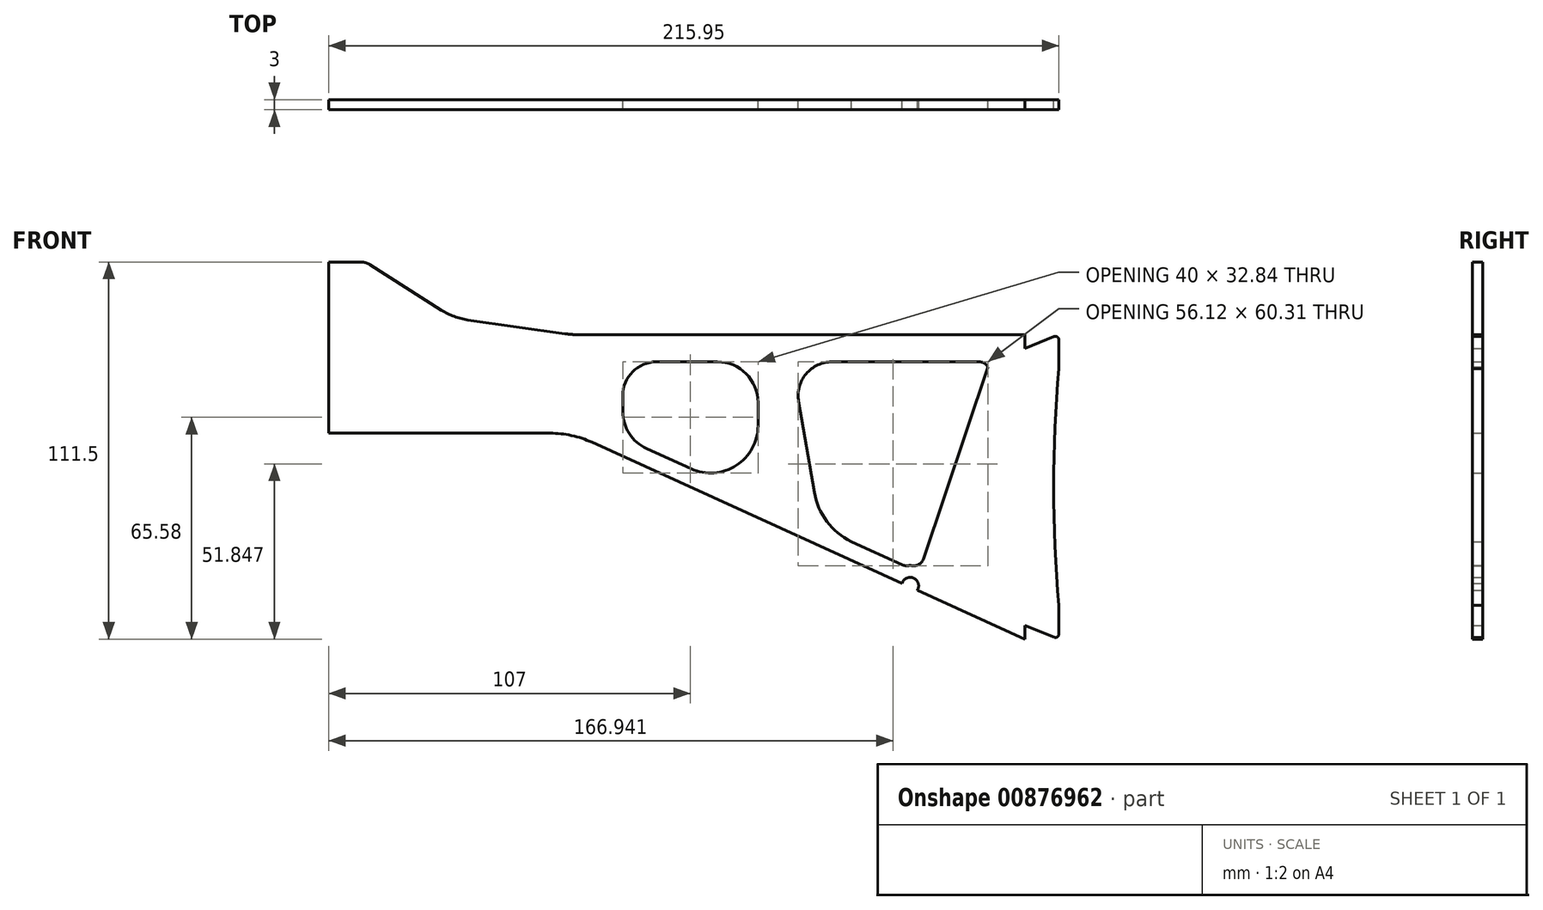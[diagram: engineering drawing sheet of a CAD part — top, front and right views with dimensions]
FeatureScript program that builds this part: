
annotation { "Feature Type Name" : "Feature", "Feature Type Description" : "" }
export const myFeature = defineFeature(function(context is Context, id is Id, definition is map)
    precondition{}
    {
        {
            var Q0;
            Q0=qCreatedBy(makeId("Front.planeOp"),FACE);
            var sketch = newSketch(context, id + "F0", { "sketchPlane" : qUnion([Q0])});
            skLineSegment(sketch, "E0", {"start": v(0, 0) * mm, "end": v(0, -50.6) * mm});
            skLineSegment(sketch, "E1", {"start": v(0, 0) * mm, "end": v(9.55, 0) * mm});
            skLineSegment(sketch, "E2", {"start": v(12.23, -0.78) * mm, "end": v(33.37, -14.2) * mm});
            skLineSegment(sketch, "E3", {"start": v(41.26, -17.1) * mm, "end": v(69.89, -21.2) * mm});
            skLineSegment(sketch, "E4", {"start": v(74.13, -21.5) * mm, "end": v(205.95, -21.5) * mm});
            skLineSegment(sketch, "E5", {"start": v(205.95, -21.5) * mm, "end": v(205.95, -25.5) * mm});
            skLineSegment(sketch, "E6", {"start": v(205.95, -25.5) * mm, "end": v(214.58, -22.05) * mm});
            skLineSegment(sketch, "E7", {"start": v(215.95, -22.98) * mm, "end": v(215.95, -31.5) * mm});
            skLineSegment(sketch, "E8", {"start": v(0, -50.6) * mm, "end": v(65.5, -50.6) * mm});
            skLineSegment(sketch, "E9", {"start": v(77.92, -53.3) * mm, "end": v(205.95, -111.5) * mm});
            skLineSegment(sketch, "E10", {"start": v(205.95, -111.5) * mm, "end": v(205.95, -107.5) * mm});
            skLineSegment(sketch, "E11", {"start": v(205.95, -107.5) * mm, "end": v(214.58, -110.95) * mm});
            skLineSegment(sketch, "E12", {"start": v(215.95, -110.02) * mm, "end": v(215.95, -101.5) * mm});
            skArc(sketch, "E13", {"start": v(215.95, -31.5) * mm, "mid": v(214.42, -66.5) * mm, "end": v(215.95, -101.5) * mm});
            skPoint(sketch, "E14.visualSharp", {"position": v(11, 0) * mm});
            skArc(sketch, "E14.filletArc", {"start": v(12.23, -0.78) * mm, "mid": v(10.94, -0.2) * mm, "end": v(9.55, 0) * mm});
            skPoint(sketch, "E15.visualSharp", {"position": v(37, -16.5) * mm});
            skArc(sketch, "E15.filletArc", {"start": v(33.37, -14.2) * mm, "mid": v(37.16, -16.07) * mm, "end": v(41.26, -17.1) * mm});
            skPoint(sketch, "E16.visualSharp", {"position": v(72, -21.5) * mm});
            skArc(sketch, "E16.filletArc", {"start": v(69.89, -21.2) * mm, "mid": v(72, -21.42) * mm, "end": v(74.13, -21.5) * mm});
            skPoint(sketch, "E17.visualSharp", {"position": v(72, -50.6) * mm});
            skArc(sketch, "E17.filletArc", {"start": v(77.92, -53.3) * mm, "mid": v(71.85, -51.3) * mm, "end": v(65.5, -50.6) * mm});
            skPoint(sketch, "E18.visualSharp", {"position": v(215.95, -21.5) * mm});
            skArc(sketch, "E18.filletArc", {"start": v(215.95, -22.98) * mm, "mid": v(215.5, -22.15) * mm, "end": v(214.58, -22.05) * mm});
            skPoint(sketch, "E19.visualSharp", {"position": v(215.95, -111.5) * mm});
            skArc(sketch, "E19.filletArc", {"start": v(214.58, -110.95) * mm, "mid": v(215.5, -110.85) * mm, "end": v(215.95, -110.02) * mm});
            skPoint(sketch, "E20", {"position": v(87, -29.5) * mm});
            skLineSegment(sketch, "E21", {"start": v(97, -29.5) * mm, "end": v(115, -29.5) * mm});
            skLineSegment(sketch, "E22", {"start": v(94.03, -55.13) * mm, "end": v(107.2, -61.12) * mm});
            skLineSegment(sketch, "E23", {"start": v(127, -48.38) * mm, "end": v(127, -41.5) * mm});
            skLineSegment(sketch, "E24", {"start": v(87, -39.5) * mm, "end": v(87, -44.2) * mm});
            skArc(sketch, "E25.filletArc", {"start": v(97, -29.5) * mm, "mid": v(89.93, -32.43) * mm, "end": v(87, -39.5) * mm});
            skPoint(sketch, "E26.visualSharp", {"position": v(87, -51.94) * mm});
            skArc(sketch, "E26.filletArc", {"start": v(87, -44.2) * mm, "mid": v(88.91, -50.7) * mm, "end": v(94.03, -55.13) * mm});
            skPoint(sketch, "E27.visualSharp", {"position": v(127, -70.12) * mm});
            skArc(sketch, "E27.filletArc", {"start": v(107.2, -61.12) * mm, "mid": v(120.58, -60.15) * mm, "end": v(127, -48.38) * mm});
            skPoint(sketch, "E28.visualSharp", {"position": v(127, -29.5) * mm});
            skArc(sketch, "E28.filletArc", {"start": v(127, -41.5) * mm, "mid": v(123.49, -33.01) * mm, "end": v(115, -29.5) * mm});
            skPoint(sketch, "E29", {"position": v(137, -29.5) * mm});
            skLineSegment(sketch, "E30", {"start": v(148.87, -29.5) * mm, "end": v(192.4, -29.5) * mm});
            skLineSegment(sketch, "E31", {"start": v(139.02, -41.2) * mm, "end": v(143.65, -68.08) * mm});
            skPoint(sketch, "E32", {"position": v(172, -95.74) * mm});
            skArc(sketch, "E33.filletArc", {"start": v(148.87, -29.5) * mm, "mid": v(141.22, -33.06) * mm, "end": v(139.02, -41.2) * mm});
            skPoint(sketch, "E34.visualSharp", {"position": v(145, -75.92) * mm});
            skArc(sketch, "E34.filletArc", {"start": v(143.65, -68.08) * mm, "mid": v(147.35, -76.67) * mm, "end": v(154.55, -82.64) * mm});
            skPoint(sketch, "E35.visualSharp", {"position": v(195.95, -29.5) * mm});
            skArc(sketch, "E35.filletArc", {"start": v(195, -31) * mm, "mid": v(193.9, -29.9) * mm, "end": v(192.4, -29.5) * mm});
            skCircle(sketch, "E36", {"center": v(172, -95.74) * mm, "radius": 2.5 * mm});
            skArc(sketch, "E37", {"start": v(171.3, -89.78) * mm, "mid": v(172.01, -89.74) * mm, "end": v(172.73, -89.79) * mm});
            skLineSegment(sketch, "E38", {"start": v(154.55, -82.64) * mm, "end": v(169.71, -89.54) * mm});
            skLineSegment(sketch, "E39", {"start": v(175.93, -87.76) * mm, "end": v(195, -31) * mm});
            skPoint(sketch, "E40.visualSharp", {"position": v(170.56, -89.92) * mm});
            skArc(sketch, "E40.filletArc", {"start": v(169.71, -89.54) * mm, "mid": v(170.5, -89.77) * mm, "end": v(171.3, -89.78) * mm});
            skPoint(sketch, "E41.visualSharp", {"position": v(175, -90.55) * mm});
            skArc(sketch, "E41.filletArc", {"start": v(172.73, -89.79) * mm, "mid": v(174.7, -89.35) * mm, "end": v(175.93, -87.76) * mm});
            skSolve(sketch);
        }
        {
            var Q0;
            Q0=makeQuery(id+"F0.imprint","IMPRINT",FACE,{"disambiguationData":[TD([[makeQuery(id+"F0.imprint","IMPRINT",EDGE,{"derivedFrom":sQuery(id+"F0.wireOp",EDGE,"E0")}),1.0]])]});
            extrude(context, id + "F1", {"entities" : qUnion([Q0]), "depth" : 3 * mm, "offsetDistance" : 25 * mm});
        }
    });
